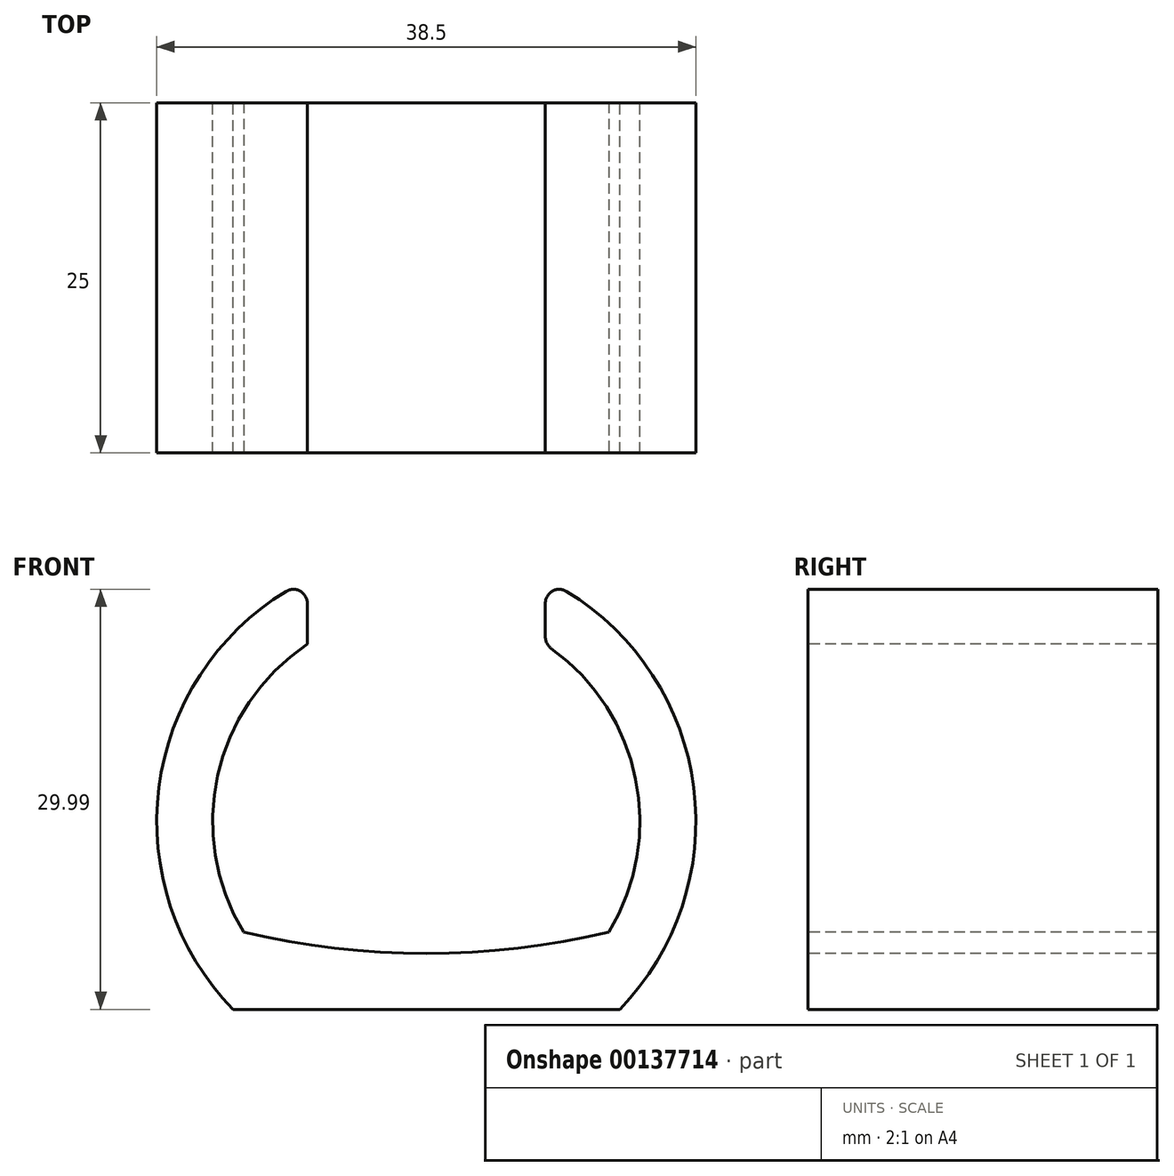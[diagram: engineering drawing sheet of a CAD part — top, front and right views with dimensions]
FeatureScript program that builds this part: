
annotation { "Feature Type Name" : "Feature", "Feature Type Description" : "" }
export const myFeature = defineFeature(function(context is Context, id is Id, definition is map)
    precondition{}
    {
        {
            var Q0;
            Q0=qCreatedBy(makeId("Front.planeOp"),FACE);
            var sketch = newSketch(context, id + "F0", { "sketchPlane" : qUnion([Q0])});
            skArc(sketch, "E0", {"start": v(12, -9.41) * mm, "mid": v(0, 15.25) * mm, "end": v(-12, -9.41) * mm});
            skLineSegment(sketch, "E1", {"start": v(-12, -9.41) * mm, "end": v(12, -9.41) * mm});
            skArc(sketch, "E2.0", {"start": v(13.8, -13.41) * mm, "mid": v(0, 19.25) * mm, "end": v(-13.8, -13.41) * mm});
            skLineSegment(sketch, "E2.1", {"start": v(-13.8, -13.41) * mm, "end": v(13.8, -13.41) * mm});
            skLineSegment(sketch, "E3", {"start": v(0, 0) * mm, "end": v(0, -9.41) * mm, "construction": true});
            skSolve(sketch);
        }
        {
            var Q0;
            Q0=qSketchRegion(id+"F0",true);
            extrude(context, id + "F1", {"entities" : qUnion([Q0]), "depth" : 25 * mm});
        }
        {
            var Q0;
            Q0=makeQuery(id+"F1.opExtrude","CAP_FACE",FACE,{"disambiguationData":[OSD([sQuery(id+"F0.wireOp",EDGE,"E0"),sQuery(id+"F0.wireOp",EDGE,"E1"),sQuery(id+"F0.wireOp",EDGE,"E2.0"),sQuery(id+"F0.wireOp",EDGE,"E2.1")])],"isStart":false});
            var sketch = newSketch(context, id + "F2", { "sketchPlane" : qUnion([Q0])});
            skLineSegment(sketch, "E4.bottom", {"start": v(-8.5, 19.25) * mm, "end": v(8.5, 19.25) * mm});
            skLineSegment(sketch, "E4.top", {"start": v(-8.5, 12.66) * mm, "end": v(8.5, 12.66) * mm});
            skLineSegment(sketch, "E4.left", {"start": v(-8.5, 19.25) * mm, "end": v(-8.5, 12.66) * mm});
            skLineSegment(sketch, "E4.right", {"start": v(8.5, 19.25) * mm, "end": v(8.5, 12.66) * mm});
            skLineSegment(sketch, "E5", {"start": v(0, 0) * mm, "end": v(0, -13.41) * mm, "construction": true});
            skSolve(sketch);
        }
        {
            var Q0;
            Q0=qSketchRegion(id+"F2",true);
            extrude(context, id + "F3", {"entities" : qUnion([Q0]), "operationType" : NewBodyOperationType.REMOVE, "endBound" : BoundingType.THROUGH_ALL, "oppositeDirection" : true, "depth" : 25 * mm});
        }
        {
            var Q0;
            Q0=makeQuery(id+"F3.boolean.opBoolean","INTERSECT",EDGE,{"derivedFrom":[makeQuery(id+"F1.opExtrude","SWEPT_FACE",FACE,{"disambiguationData":[OSD([sQuery(id+"F0.wireOp",EDGE,"E2.0")])]}),makeQuery(id+"F3.opExtrude","SWEPT_FACE",FACE,{"disambiguationData":[OSD([sQuery(id+"F2.wireOp",EDGE,"E4.left")])]})]});
            var Q1;
            Q1=makeQuery(id+"F3.boolean.opBoolean","COPY",EDGE,{"derivedFrom":makeQuery(id+"F3.opExtrude","SWEPT_EDGE",EDGE,{"disambiguationData":[OSD([sQuery(id+"F0.wireOp",EDGE,"E0"),sQuery(id+"F2.wireOp",EDGE,"E4.top"),sQuery(id+"F2.wireOp",EDGE,"E4.left")])]})});
            var Q2;
            Q2=makeQuery(id+"F3.boolean.opBoolean","INTERSECT",EDGE,{"derivedFrom":[makeQuery(id+"F1.opExtrude","SWEPT_FACE",FACE,{"disambiguationData":[OSD([sQuery(id+"F0.wireOp",EDGE,"E2.0")])]}),makeQuery(id+"F3.opExtrude","SWEPT_FACE",FACE,{"disambiguationData":[OSD([sQuery(id+"F2.wireOp",EDGE,"E4.right")])]})]});
            var Q3;
            Q3=makeQuery(id+"F3.boolean.opBoolean","COPY",EDGE,{"derivedFrom":makeQuery(id+"F3.opExtrude","SWEPT_EDGE",EDGE,{"disambiguationData":[OSD([sQuery(id+"F0.wireOp",EDGE,"E0"),sQuery(id+"F2.wireOp",EDGE,"E4.top"),sQuery(id+"F2.wireOp",EDGE,"E4.right")])]})});
            fillet(context, id + "F4", {"entities" : qUnion([Q0, Q1, Q2, Q3]), "radius" : 1 * mm, "tangentPropagation" : true, "allowEdgeOverflow" : false});
        }
        {
            var Q0;
            Q0=makeQuery(id+"F1.opExtrude","CAP_FACE",FACE,{"disambiguationData":[OSD([sQuery(id+"F0.wireOp",EDGE,"E0"),sQuery(id+"F0.wireOp",EDGE,"E1"),sQuery(id+"F0.wireOp",EDGE,"E2.0"),sQuery(id+"F0.wireOp",EDGE,"E2.1")])],"isStart":false});
            var sketch = newSketch(context, id + "F5", { "sketchPlane" : qUnion([Q0])});
            skArc(sketch, "E6", {"start": v(-13.04, -7.91) * mm, "mid": v(0, -9.41) * mm, "end": v(13.04, -7.91) * mm});
            skArc(sketch, "E7.0", {"start": v(-13.04, -7.91) * mm, "mid": v(-12.54, -8.68) * mm, "end": v(-12, -9.41) * mm});
            skArc(sketch, "E7.1", {"start": v(12, -9.41) * mm, "mid": v(12.54, -8.68) * mm, "end": v(13.04, -7.91) * mm});
            skLineSegment(sketch, "E7.2", {"start": v(-12, -9.41) * mm, "end": v(12, -9.41) * mm});
            skPoint(sketch, "E8.orphan", {"position": v(-8.92, 12.37) * mm});
            skPoint(sketch, "E9.orphan", {"position": v(8.92, 12.37) * mm});
            skSolve(sketch);
        }
        {
            var Q0;
            Q0=qSketchRegion(id+"F5",true);
            var Q1;
            Q1=makeQuery(id+"F1.opExtrude","CAP_FACE",FACE,{"disambiguationData":[OSD([sQuery(id+"F0.wireOp",EDGE,"E0"),sQuery(id+"F0.wireOp",EDGE,"E1"),sQuery(id+"F0.wireOp",EDGE,"E2.0"),sQuery(id+"F0.wireOp",EDGE,"E2.1")])],"isStart":true});
            extrude(context, id + "F6", {"entities" : qUnion([Q0]), "operationType" : NewBodyOperationType.ADD, "endBound" : BoundingType.UP_TO_SURFACE, "oppositeDirection" : true, "endBoundEntityFace" : qUnion([Q1]), "depth" : 25 * mm});
        }
    });
